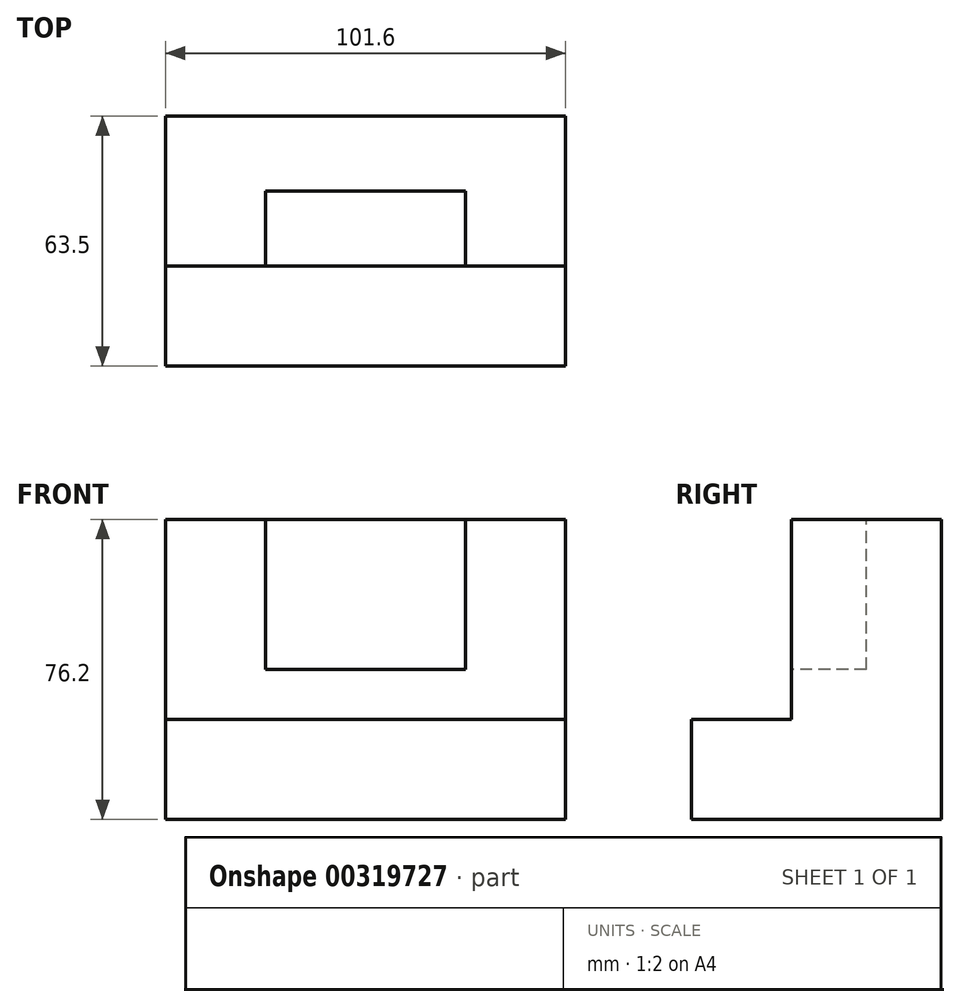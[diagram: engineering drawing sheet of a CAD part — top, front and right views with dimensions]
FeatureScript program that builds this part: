
annotation { "Feature Type Name" : "Feature", "Feature Type Description" : "" }
export const myFeature = defineFeature(function(context is Context, id is Id, definition is map)
    precondition{}
    {
        {
            var Q0;
            Q0=qCreatedBy(makeId("Right.planeOp"),FACE);
            var sketch = newSketch(context, id + "F0", { "sketchPlane" : qUnion([Q0])});
            skLineSegment(sketch, "E0", {"start": v(-11.54, 35.18) * mm, "end": v(26.56, 35.18) * mm});
            skLineSegment(sketch, "E1", {"start": v(26.56, 35.18) * mm, "end": v(26.56, -41.02) * mm});
            skLineSegment(sketch, "E2", {"start": v(26.56, -41.02) * mm, "end": v(-36.94, -41.02) * mm});
            skLineSegment(sketch, "E3", {"start": v(-36.94, -41.02) * mm, "end": v(-36.94, -15.62) * mm});
            skLineSegment(sketch, "E4", {"start": v(-36.94, -15.62) * mm, "end": v(-11.54, -15.62) * mm});
            skLineSegment(sketch, "E5", {"start": v(-11.54, -15.62) * mm, "end": v(-11.54, 35.18) * mm});
            skSolve(sketch);
        }
        {
            var Q0;
            Q0=makeQuery(id+"F0.imprint","IMPRINT",FACE,{"disambiguationData":[TD([[makeQuery(id+"F0.imprint","IMPRINT",EDGE,{"derivedFrom":sQuery(id+"F0.wireOp",EDGE,"E0")}),-1.0]])]});
            extrude(context, id + "F1", {"entities" : qUnion([Q0]), "oppositeDirection" : true, "depth" : 101.6 * mm});
        }
        {
            var Q0;
            Q0=makeQuery(id+"F1.opExtrude","SWEPT_FACE",FACE,{"disambiguationData":[OSD([sQuery(id+"F0.wireOp",EDGE,"E5")])]});
            var sketch = newSketch(context, id + "F2", { "sketchPlane" : qUnion([Q0])});
            skLineSegment(sketch, "E6", {"start": v(-76.2, 16.17) * mm, "end": v(-76.2, -2.92) * mm});
            skLineSegment(sketch, "E7", {"start": v(-76.2, -2.92) * mm, "end": v(-25.4, -2.92) * mm});
            skLineSegment(sketch, "E8", {"start": v(-25.4, -2.92) * mm, "end": v(-25.4, 35.18) * mm});
            skLineSegment(sketch, "E9", {"start": v(-25.4, 35.18) * mm, "end": v(-76.2, 35.18) * mm});
            skLineSegment(sketch, "E10", {"start": v(-76.2, 35.18) * mm, "end": v(-76.2, -2.92) * mm});
            skSolve(sketch);
        }
        {
            var Q0;
            {var subQ3=sQuery(id+"F2.wireOp",EDGE,"E7");Q0=makeQuery(id+"F2.imprint","IMPRINT",FACE,{"disambiguationData":[TD([[makeQuery(id+"F2.imprint","IMPRINT",EDGE,{"derivedFrom":subQ3}),1.0]])]});}
            extrude(context, id + "F3", {"entities" : qUnion([Q0]), "operationType" : NewBodyOperationType.REMOVE, "oppositeDirection" : true, "depth" : 19.05 * mm});
        }
    });
